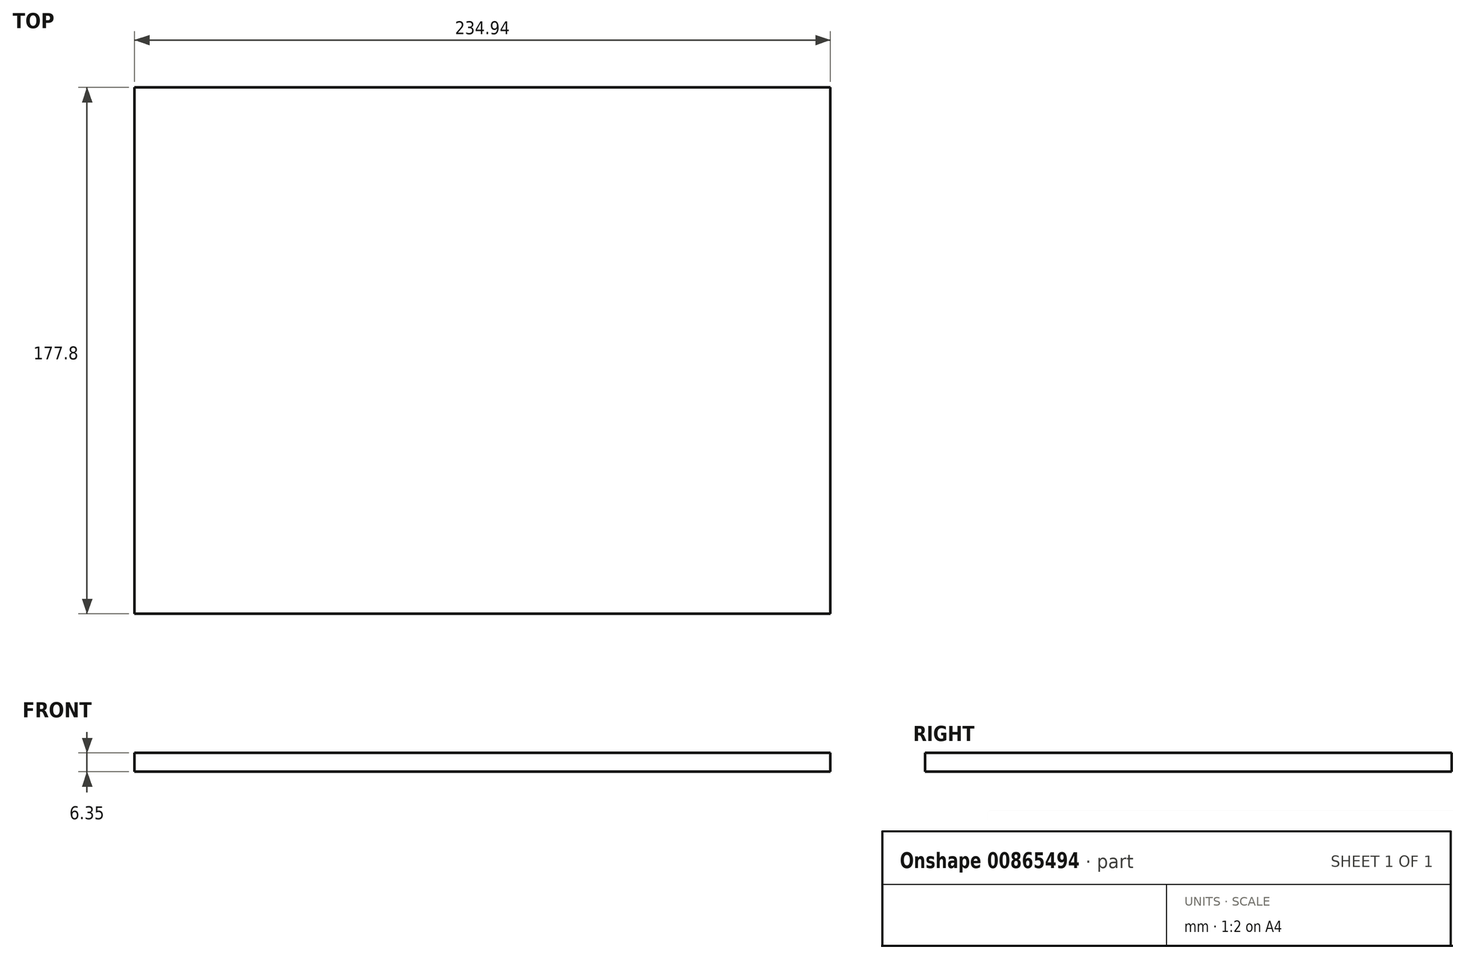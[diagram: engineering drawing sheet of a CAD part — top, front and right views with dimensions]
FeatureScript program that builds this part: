
annotation { "Feature Type Name" : "Feature", "Feature Type Description" : "" }
export const myFeature = defineFeature(function(context is Context, id is Id, definition is map)
    precondition{}
    {
        {
            var Q0;
            Q0=qCreatedBy(makeId("Top.planeOp"),FACE);
            var sketch = newSketch(context, id + "F0", { "sketchPlane" : qUnion([Q0])});
            skLineSegment(sketch, "E0.bottom", {"start": v(-117.48, 88.9) * mm, "end": v(117.48, 88.9) * mm});
            skLineSegment(sketch, "E0.top", {"start": v(-117.47, -88.9) * mm, "end": v(117.48, -88.9) * mm});
            skLineSegment(sketch, "E0.left", {"start": v(-117.48, 88.9) * mm, "end": v(-117.47, -88.9) * mm});
            skLineSegment(sketch, "E0.right", {"start": v(117.48, 88.9) * mm, "end": v(117.48, -88.9) * mm});
            skPoint(sketch, "E0.middle", {"position": v(0, 0) * mm});
            skSolve(sketch);
        }
        {
            var Q0;
            Q0 = qSketchRegion(id + "F0", true);
            extrude(context, id + "F1", {"entities" : qUnion([Q0]), "depth" : 6.35 * mm, "offsetDistance" : 25.4 * mm});
        }
    });
